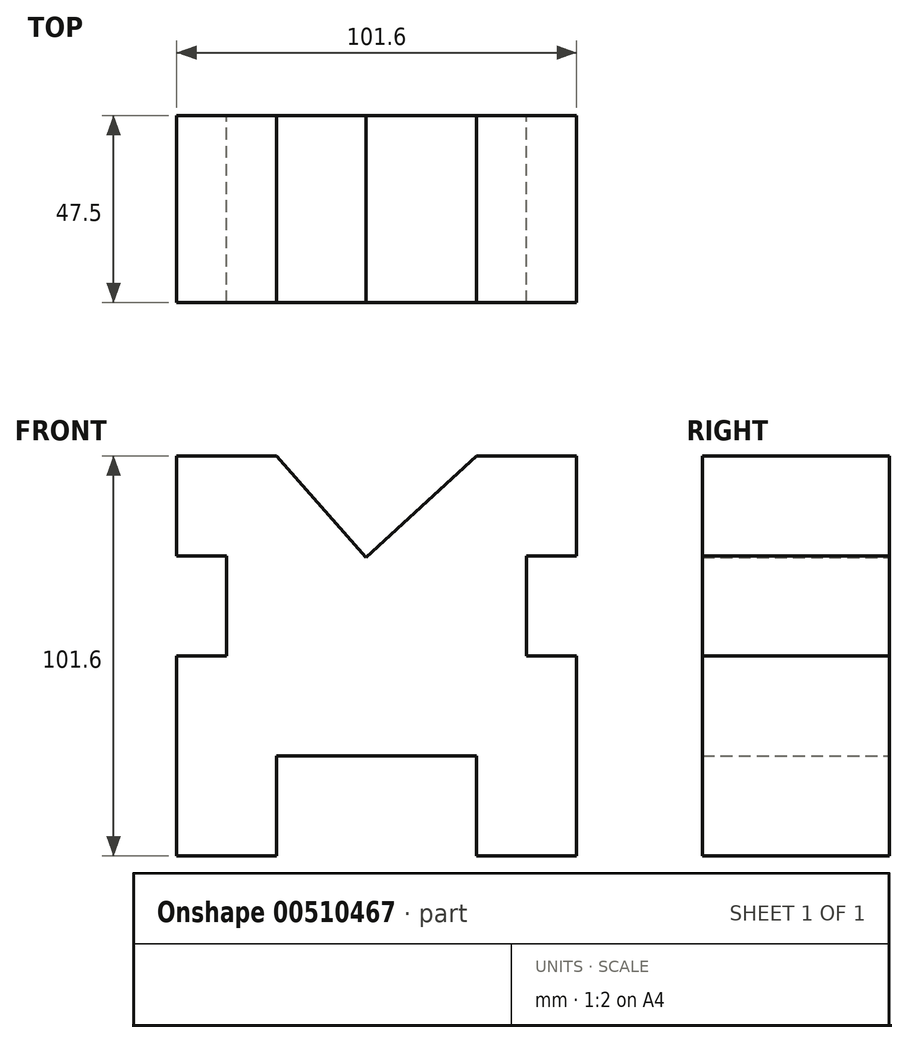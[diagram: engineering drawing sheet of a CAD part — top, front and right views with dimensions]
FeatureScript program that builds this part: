
annotation { "Feature Type Name" : "Feature", "Feature Type Description" : "" }
export const myFeature = defineFeature(function(context is Context, id is Id, definition is map)
    precondition{}
    {
        {
            var Q0;
            Q0=qCreatedBy(makeId("Front.planeOp"),FACE);
            var sketch = newSketch(context, id + "F0", { "sketchPlane" : qUnion([Q0])});
            skLineSegment(sketch, "E0", {"start": v(-13.75, 11.8) * mm, "end": v(-26.45, 11.8) * mm});
            skLineSegment(sketch, "E1", {"start": v(-26.45, 11.8) * mm, "end": v(-26.45, -13.6) * mm});
            skLineSegment(sketch, "E2", {"start": v(-26.45, -13.6) * mm, "end": v(-13.75, -13.6) * mm});
            skLineSegment(sketch, "E3", {"start": v(-13.75, -13.6) * mm, "end": v(-13.75, -64.4) * mm});
            skLineSegment(sketch, "E4", {"start": v(-13.75, -64.4) * mm, "end": v(-39.15, -64.4) * mm});
            skLineSegment(sketch, "E5", {"start": v(-39.15, -64.4) * mm, "end": v(-39.15, -39) * mm});
            skLineSegment(sketch, "E6", {"start": v(-39.15, -39) * mm, "end": v(-89.95, -39) * mm});
            skLineSegment(sketch, "E7", {"start": v(-89.95, -39) * mm, "end": v(-89.95, -64.4) * mm});
            skLineSegment(sketch, "E8", {"start": v(-89.95, -64.4) * mm, "end": v(-115.35, -64.4) * mm});
            skLineSegment(sketch, "E9", {"start": v(-115.35, -64.4) * mm, "end": v(-115.35, -13.6) * mm});
            skLineSegment(sketch, "E10", {"start": v(-115.35, -13.6) * mm, "end": v(-102.65, -13.6) * mm});
            skPoint(sketch, "E10.endSnap0", {"position": v(-20.1, -13.6) * mm});
            skLineSegment(sketch, "E11", {"start": v(-102.65, -13.6) * mm, "end": v(-102.65, 11.8) * mm});
            skLineSegment(sketch, "E12", {"start": v(-102.65, 11.8) * mm, "end": v(-115.35, 11.8) * mm});
            skLineSegment(sketch, "E13", {"start": v(-115.35, 11.8) * mm, "end": v(-115.35, 37.2) * mm});
            skLineSegment(sketch, "E14", {"start": v(-13.75, 11.8) * mm, "end": v(-13.75, 37.2) * mm});
            skLineSegment(sketch, "E15", {"start": v(-115.35, 37.2) * mm, "end": v(-89.95, 37.2) * mm});
            skLineSegment(sketch, "E16", {"start": v(-13.75, 37.2) * mm, "end": v(-39.15, 37.2) * mm});
            skLineSegment(sketch, "E17", {"start": v(-39.15, 37.2) * mm, "end": v(-67.21, 11.44) * mm});
            skLineSegment(sketch, "E18", {"start": v(-67.21, 11.44) * mm, "end": v(-89.95, 37.2) * mm});
            skSolve(sketch);
        }
        {
            var Q0;
            Q0=makeQuery(id+"F0.imprint","IMPRINT",FACE,{"disambiguationData":[TD([[makeQuery(id+"F0.imprint","IMPRINT",EDGE,{"derivedFrom":sQuery(id+"F0.wireOp",EDGE,"E0")}),-1.0]])]});
            extrude(context, id + "F1", {"entities" : qUnion([Q0]), "depth" : 47.5 * mm, "offsetDistance" : 25.4 * mm});
        }
    });
